# Revit family: CleanLine serisi duş kanalları için Geberit montaj seti, girişte 65–90 mm şap yüksekliği için_PRO_170944
name_source: partatom
category: Plumbing Fixtures
revit_build: Autodesk Revit 2018 (Build: 20190510_1515(x64)
units: mm (PartAtom-declared; Revit-internal decimal feet)

## family parameters
Always vertical = Yes
Cut with Voids When Loaded = No
OmniClass Number = 23.70.50.21.24
OmniClass Title = Waste Water Drains
Part Type = Normal
Room Calculation Point = Yes
Round Connector Dimension = Use Diameter
Shared = No
Work Plane-Based = No

## types (1)
- 154.152.00.1 CleanLine serisi duş kanalları için Geberit montaj seti, girişte 65–90 mm şap yüksekliği için
    Application purposes = CleanLine serisi Geberit duş kanallarında drenaj için
Kompozit contalar için
Girişte ≥ 65 mm şap yükseklikleri için
    Application range = Floor drainage system
    Article number key = 154.152.00.1
    B = 130 mm  [stored 0.426509 ft]
    BIM Content Version = GEB MG 1.2
    BIM Content revision date = 2020.04.30
    Brand = Geberit
    CW Connection = No
    Characteristics = EN 1253'ün gerekliliklerinden farklı olarak, sifon yüksekliği sadece 30 mm'dir.
Önceden monte edilmiş izolasyon bezi
Sızdırmazlık sistemleri bağlantısı için 10 cm çevreleyen izolasyon bezi
Akustik izolasyon ve sifon bağlantısı için EPS ana ünite
    Connection diameter 1 = 40 mm  [stored 0.131234 ft]
    Description = CleanLine serisi duş kanalları için Geberit montaj seti, girişte 65–90 mm şap yüksekliği için
    Drenaj kapasitesi = 0.4 L/s
    EAN code basic data = 4025416364818
    GEB_culture = tr-TR
    GEB_generic_description = installation set for shower channels
    GEB_generic_manufacturer = generic
    GEB_generic_model = horizontal outlet
    GEB_imperial_engineering = No
    GEB_key_rules = 1000 [Articles.ArticlesList.Key]
2000 [Name], d[ATT_10935]
3000 [ATT_10673]
    GEB_metric_engineering = Yes
    GEB_pimversion = 22.02.12
    GEB_processing_type = T
    GEB_reference = PRO_170944
    GEB_size_max = 175 mm  [stored 0.574147 ft]
    GEB_size_min = 65 mm  [stored 0.213255 ft]
    GEB_translations = {"ATT_10673":"EAN code basic data","applicationPurposes":"Application purposes","application_range":"Application range","brandName":"Brand","characteristics":"Characteristics","content_creator":"BIM Content creator","content_date_changed":"BIM Content revision date","content_version":"BIM Content Version","key 1000":"Article number key","name":"Name","productBrand":"Product brand","type":"Type","GEB_connection_diameter1":"Connection diameter 1","angle":"Angle","ATT_10753":"Drenaj kapasitesi","fixed_material":"Main material","fixed_material_01":"Main material 01","ATT_10931":"B","ATT_10935":"d, ø","ATT_10951":"H","ATT_10952":"h","ATT_10966":"L","ATT_10969":"L1","GEB_accessories":"Accessories"}
    GEB_use_DN = Yes
    H = 65 mm  [stored 0.213255 ft]
    HW Connection = No
    IfcDescription = CleanLine serisi duş kanalları için Geberit montaj seti, girişte 65–90 mm şap yüksekliği için
    IfcExportAs = IfcSanitaryTerminal
    IfcExportType = USERDEFINED
    L = 300 mm  [stored 0.984252 ft]
    L1 = 358 mm
    LOD300 = No
    LOD400 = Yes
    Main material = Geberit_Plastic, White
    Main material 01 = Geberit_PE-HD, Black.
    Manufacturer = Geberit
    Model = d40
    Name = CleanLine serisi duş kanalları için Geberit montaj seti, girişte 65–90 mm şap yüksekliği için
    Type = d40
    Vent Connection = No
    WFU = 0
    Waste Connection = Yes
    d, ø = 40 mm  [stored 0.131234 ft]
    h = 32 mm  [stored 0.104987 ft]

note: [stored X ft] marks values corroborated as IEEE doubles in the binary element streams (Revit-internal decimal feet)

## geometry (parser evidence)
native form markers: Blend x2, Sweep x4
no freeform markers — native parametric forms only
